# Revit family: PGR_Noken_WtrSplyFitngsForThrmstcMxngVlves_LIBERTY
name_source: partatom
category: Plumbing Fixtures
revit_build: Autodesk Revit 2017 (Build: 20190508_0315(x64)
units: mm (PartAtom-declared; Revit-internal decimal feet)

## family parameters
Always vertical = Yes
Cut with Voids When Loaded = No
OmniClass Number = 23.45.55.17
OmniClass Title = Mixing Faucets
Part Type = Normal
Room Calculation Point = No
Round Connector Dimension = Use Diameter
Shared = No
Work Plane-Based = No

## types (1)
- LIBERTY CROMO - 100064126
    AccessibilityPerformance = See ProductInformation for technical PDF
    ApplicationType = Shower
    AssetType = Fixed
    BIMObjectName = PGR_Noken_WaterSupplyFittingsForBath_Liberty _Chrome-28x50x50mm-100064216
    BodyMaterial = Brass
    Category = Pr_40_20_87_09: Bath taps
    CloseOffRating = 0.0 Pa
    CodePerformance = EN 817, EN 248
    Collection = Liberty
    Color = Chrome
    Description = Liberty. Water supply. Material brass, finish chrome plated, nominal length 50 mm, nominal width 28 mm, nominal height 50 mm, net product weight 1,4 kg . UNE EN 817, UNE EN 248
    DurationUnit = year
    FaucetFunction = Cold
    FaucetOperation = Other
    Features = See ProductInformation for tecnical PDF
    Finish = Chrome
    FlowCoefficient = 0
    IfcExportAs = IfcValveType
    IfcExportType = Faucet
    InletConnectionSize = 0 mm  [stored 0 ft]
    ManufacturerURL = www.noken.com
    Material = Brass
    MaterialMetal = PGR_Noken_Brass_Chrome
    Model = 100064216
    ModelNumber = 100064216
    ModelReference = TOMA DE AGUA LIBERTY
    NBSDescription = Water supply fittings for baths
    NBSReference = 45-35-70/315
    Name = WaterSupplyFittingsForBath_Liberty _Chrome-28x50x50mm-100064216
    NettWeight = 4
    NominalHeight = 50 mm  [stored 0.164042 ft]
    NominalLength = 50 mm  [stored 0.164042 ft]
    NominalWidth = 28 mm  [stored 0.0918635 ft]
    NumberOfConnections = 2
    OutletConnectionSize = 0 mm  [stored 0 ft]
    ProductInformation = http://calidad.info-grupo.com:8081
    Reference = -
    Size = 28x50x50mm
    Status = UNSET
    SustainabilityPerformance = See ProductInformation for technical PDF
    TechnicalDrawing = See ProductInformation for technical PDF
    TestPressure = 0.0 Pa
    Type Image = 100064216.jpg
    URL = www.noken.com
    Uniclass2015Code = Pr_40_20_87_09
    Uniclass2015Title = Bath taps
    ValveMechanism = UNSET
    ValveOperation = Other
    ValvePattern = UNSET
    WarrantyDescription = See ProductInformation for technical PDF
    WarrantyDurationUnit = year

note: [stored X ft] marks values corroborated as IEEE doubles in the binary element streams (Revit-internal decimal feet)

## geometry (parser evidence)
native form markers: Blend x2, Sweep x3
no freeform markers — native parametric forms only
